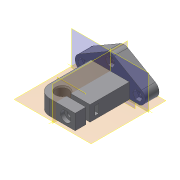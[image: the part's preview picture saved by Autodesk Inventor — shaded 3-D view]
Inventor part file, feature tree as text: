
AUTODESK INVENTOR PART (.ipt)
format: ipt  version: 2015 SP2 (Build 190223200, 223)  size: 404,480 bytes
history: native  units: mm
features: extrude x10, sketch x10, projected_geometry x3, plane x2, fillet x2, other x1, mirror x1, chamfer x1
ambient origin geometry x8: Origin, YZ Plane, XZ Plane, XY Plane, X Axis, Y Axis, Z Axis, Center Point
bodies: Body1 (feature_tree)
feature tree (30):
  other  "Sólido1"
  extrude  "Extrusión1"  Depth=39.25mm
  extrude  "Extrusión3"  Depth=5.244714mm
  plane  "Plano de trabajo2"
  extrude  "Extrusión5"  Depth=17.0mm
  extrude  "Extrusión6"  Depth=10.0mm
  plane  "Plano de trabajo3"
  extrude  "Extrusión9"  Depth=3.75mm
  extrude  "Extrusión10"  Depth=6.2mm
  mirror  "Simetría1"
  extrude  "Extrusión11"  Depth=6.2mm
  extrude  "Extrusión12"  [1 undecoded]
  extrude  "Extrusión13"  Depth=6.235mm
  extrude  "Extrusión16"  Depth=10.0mm TaperAngle=0.0deg
  fillet  "Empalme3"  Radius=1.5mm
  chamfer  "Chamfer1"  Distance=5.0mm
  fillet  "Empalme2"  Radius=7.75mm
  sketch  "Boceto1"  dims[d0=27.75mm d1=39.25mm]
  sketch  "Boceto3"  dims[d2=11.0mm d3=0.0mm d21=5.244714mm]
  sketch  "Boceto5"  dims[d23=39.75mm d25=17.0mm]
  projected_geometry  "Contorno proyectado2"
  sketch  "Boceto6"  dims[d26=10.0mm d27=0.0mm d33=3.75mm]
  projected_geometry  "Contorno proyectado3"
  sketch  "Boceto9"  dims[d34=3.75mm d35=3.75mm]
  projected_geometry  "Contorno proyectado5"
  sketch  "Boceto10"  dims[d36=2.8mm d37=0.0mm d38=6.2mm]
  sketch  "Boceto11"  dims[d39=6.2mm d40=6.2mm]
  sketch  "Boceto12"  dims[d41=2.8mm d42=0.0mm d51=-15.71mm]
  sketch  "Boceto13"  dims[d53=120.0deg d56=6.235mm]
  sketch  "Boceto14"  dims[d57=8.781572mm d58=2.8mm d59=0.0mm d60=1.5mm d61=5.0mm d63=7.75mm d64=4.4mm d65=10.0mm d66=0.0mm d67=10.0mm d68=0.0mm d69=7.5mm d70=5.5mm d71=6.8mm d72=2.8mm d73=0.0mm d74=3.75mm d75=26.4mm d76=0.0mm d80=30.0mm d81=90.0deg d84=10.0mm d85=0.0mm d86=2.0mm d87=0.0mm d88=0.5mm d89=18.5mm d90=9.25mm d91=1.0mm d92=2.0mm d93=30.0deg]
note: 1 required parameter value undecoded (feature->parameter linkage not recoverable at this tier; creation-order binding heuristic only, values carry confidence <= 0.55)
